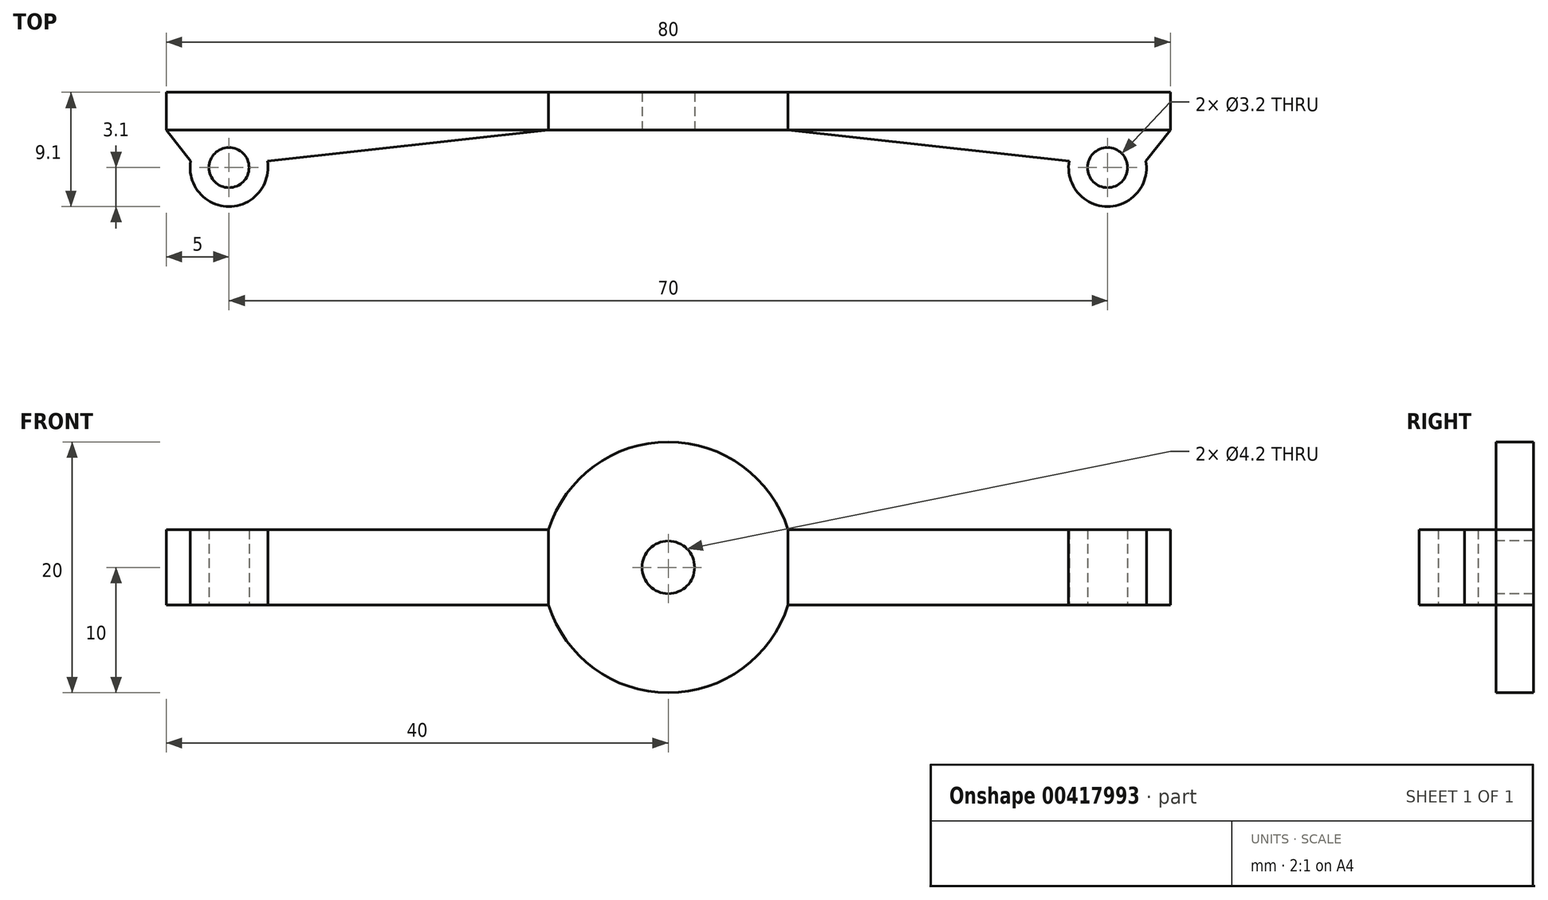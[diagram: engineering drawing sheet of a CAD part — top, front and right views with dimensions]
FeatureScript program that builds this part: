
annotation { "Feature Type Name" : "Feature", "Feature Type Description" : "" }
export const myFeature = defineFeature(function(context is Context, id is Id, definition is map)
    precondition{}
    {
        {
            var Q0;
            Q0=qCreatedBy(makeId("Front.planeOp"),FACE);
            var sketch = newSketch(context, id + "F0", { "sketchPlane" : qUnion([Q0])});
            skCircle(sketch, "E0", {"center": v(0, 0) * mm, "radius": 10 * mm});
            skLineSegment(sketch, "E1.bottom", {"start": v(40, -3) * mm, "end": v(-40, -3) * mm});
            skLineSegment(sketch, "E1.top", {"start": v(40, 3) * mm, "end": v(-40, 3) * mm});
            skLineSegment(sketch, "E1.left", {"start": v(40, -3) * mm, "end": v(40, 3) * mm});
            skLineSegment(sketch, "E1.right", {"start": v(-40, -3) * mm, "end": v(-40, 3) * mm});
            skSolve(sketch);
        }
        {
            var Q0;
            {var subQ0=sQuery(id+"F0.wireOp",EDGE,"E1.top");var subQ1=sQuery(id+"F0.wireOp",EDGE,"E0");var subQ2=makeQuery(id+"F0.imprint","INTERSECT",VERTEX,{"disambiguationData":[OD(0.0)],"derivedFrom":[subQ1,subQ0]});Q0=makeQuery(id+"F0.imprint","IMPRINT",FACE,{"disambiguationData":[TD([[makeQuery(id+"F0.imprint","IMPRINT",EDGE,{"disambiguationData":[TD([[subQ2,-1.0]])],"derivedFrom":subQ1}),1.0]])]});}
            var Q1;
            {var subQ0=sQuery(id+"F0.wireOp",EDGE,"E1.top");var subQ1=sQuery(id+"F0.wireOp",EDGE,"E0");var subQ2=makeQuery(id+"F0.imprint","INTERSECT",VERTEX,{"disambiguationData":[OD(0.0)],"derivedFrom":[subQ1,subQ0]});Q1=makeQuery(id+"F0.imprint","IMPRINT",FACE,{"disambiguationData":[TD([[makeQuery(id+"F0.imprint","IMPRINT",EDGE,{"disambiguationData":[TD([[subQ2,1.0]])],"derivedFrom":subQ1}),1.0]])]});}
            var Q2;
            {var subQ5=sQuery(id+"F0.wireOp",EDGE,"E1.left");Q2=makeQuery(id+"F0.imprint","IMPRINT",FACE,{"disambiguationData":[TD([[makeQuery(id+"F0.imprint","IMPRINT",EDGE,{"derivedFrom":subQ5}),1.0]])]});}
            var Q3;
            {var subQ0=sQuery(id+"F0.wireOp",EDGE,"E1.bottom");var subQ1=sQuery(id+"F0.wireOp",EDGE,"E0");var subQ2=makeQuery(id+"F0.imprint","INTERSECT",VERTEX,{"disambiguationData":[OD(0.0)],"derivedFrom":[subQ1,subQ0]});Q3=makeQuery(id+"F0.imprint","IMPRINT",FACE,{"disambiguationData":[TD([[makeQuery(id+"F0.imprint","IMPRINT",EDGE,{"disambiguationData":[TD([[subQ2,-1.0]])],"derivedFrom":subQ1}),1.0]])]});}
            var Q4;
            {var subQ5=sQuery(id+"F0.wireOp",EDGE,"E1.right");Q4=makeQuery(id+"F0.imprint","IMPRINT",FACE,{"disambiguationData":[TD([[makeQuery(id+"F0.imprint","IMPRINT",EDGE,{"derivedFrom":subQ5}),-1.0]])]});}
            extrude(context, id + "F1", {"entities" : qUnion([Q0, Q1, Q2, Q3, Q4]), "depth" : 3 * mm});
        }
        {
            var Q0;
            Q0=makeQuery(id+"F1.opExtrude","CAP_FACE",FACE,{"disambiguationData":[OSD([sQuery(id+"F0.wireOp",EDGE,"E0"),sQuery(id+"F0.wireOp",EDGE,"E1.bottom"),sQuery(id+"F0.wireOp",EDGE,"E1.top"),sQuery(id+"F0.wireOp",EDGE,"E1.left"),sQuery(id+"F0.wireOp",EDGE,"E1.right")])],"isStart":false});
            var sketch = newSketch(context, id + "F2", { "sketchPlane" : qUnion([Q0])});
            skCircle(sketch, "E2", {"center": v(0, 0) * mm, "radius": 2 * mm});
            skSolve(sketch);
        }
        {
            var Q0;
            Q0=sQuery(id+"F2.wireOp",VERTEX,"E2.center");
            var Q1;
            Q1=makeQuery(id+"F1.opExtrude","SWEPT_BODY",BODY,{"disambiguationData":[OSD([sQuery(id+"F0.wireOp",EDGE,"E0"),sQuery(id+"F0.wireOp",EDGE,"E1.bottom"),sQuery(id+"F0.wireOp",EDGE,"E1.top"),sQuery(id+"F0.wireOp",EDGE,"E1.left"),sQuery(id+"F0.wireOp",EDGE,"E1.right")])]});
            hole(context, id + "F3", {"style" : HoleStyle.SIMPLE, "endStyle" : HoleEndStyle.THROUGH, "holeDiameter" : 4.2 * mm, "isTappedThrough" : true, "tappedDepth" : 12 * mm, "tapClearance" : 3, "locations" : qUnion([Q0]), "scope" : qUnion([Q1])});
        }
        {
            var Q0;
            Q0=qCreatedBy(makeId("Top.planeOp"),FACE);
            var sketch = newSketch(context, id + "F4", { "sketchPlane" : qUnion([Q0])});
            skLineSegment(sketch, "E3", {"start": v(-40, 0) * mm, "end": v(-40, -3) * mm});
            skArc(sketch, "E4.filletArc", {"start": v(-38.06, -5.49) * mm, "mid": v(-35, -9.1) * mm, "end": v(-31.94, -5.49) * mm});
            skCircle(sketch, "E5", {"center": v(-35, -6) * mm, "radius": 1.6 * mm});
            skLineSegment(sketch, "E6", {"start": v(-31.94, -5.49) * mm, "end": v(-9.54, -3) * mm});
            skLineSegment(sketch, "E7", {"start": v(-40, -3) * mm, "end": v(-38.06, -5.49) * mm});
            skLineSegment(sketch, "E8", {"start": v(-9.54, -3) * mm, "end": v(-40, -3) * mm});
            skSolve(sketch);
        }
        {
            var Q0;
            Q0 = qSketchRegion(id + "F4", true);
            var Q1;
            {var subQ0=sQuery(id+"F0.wireOp",EDGE,"E1.top");Q1=makeQuery(id+"F1.opExtrude","SWEPT_FACE",FACE,{"disambiguationData":[OSD([subQ0]),TDD([makeQuery(id+"F0.imprint","IMPRINT",EDGE,{"disambiguationData":[TD([[makeQuery(id+"F0.imprint","INTERSECT",VERTEX,{"derivedFrom":[subQ0,sQuery(id+"F0.wireOp",EDGE,"E1.right")]}),1.0]])],"derivedFrom":subQ0})])]});}
            var Q2;
            {var subQ0=sQuery(id+"F0.wireOp",EDGE,"E1.bottom");Q2=makeQuery(id+"F1.opExtrude","SWEPT_FACE",FACE,{"disambiguationData":[OSD([subQ0]),TDD([makeQuery(id+"F0.imprint","IMPRINT",EDGE,{"disambiguationData":[TD([[makeQuery(id+"F0.imprint","INTERSECT",VERTEX,{"derivedFrom":[subQ0,sQuery(id+"F0.wireOp",EDGE,"E1.right")]}),1.0]])],"derivedFrom":subQ0})])]});}
            extrude(context, id + "F5", {"entities" : qUnion([Q0]), "operationType" : NewBodyOperationType.ADD, "endBound" : BoundingType.UP_TO_SURFACE, "endBoundEntityFace" : qUnion([Q1]), "depth" : 25 * mm, "hasSecondDirection" : true, "secondDirectionBound" : SecondDirectionBoundingType.UP_TO_SURFACE, "secondDirectionOppositeDirection" : true, "secondDirectionBoundEntityFace" : qUnion([Q2]), "secondDirectionDepth" : 25 * mm});
        }
        {
            var Q0;
            Q0=makeQuery(id+"F1.opExtrude","SWEPT_BODY",BODY,{"disambiguationData":[OSD([sQuery(id+"F0.wireOp",EDGE,"E0"),sQuery(id+"F0.wireOp",EDGE,"E1.bottom"),sQuery(id+"F0.wireOp",EDGE,"E1.top"),sQuery(id+"F0.wireOp",EDGE,"E1.left"),sQuery(id+"F0.wireOp",EDGE,"E1.right")])]});
            var Q1;
            Q1=qCreatedBy(makeId("Right.planeOp"),FACE);
            mirror(context, id + "F6", {"entities" : qUnion([Q0]), "mirrorPlane" : qUnion([Q1])});
        }
    });
